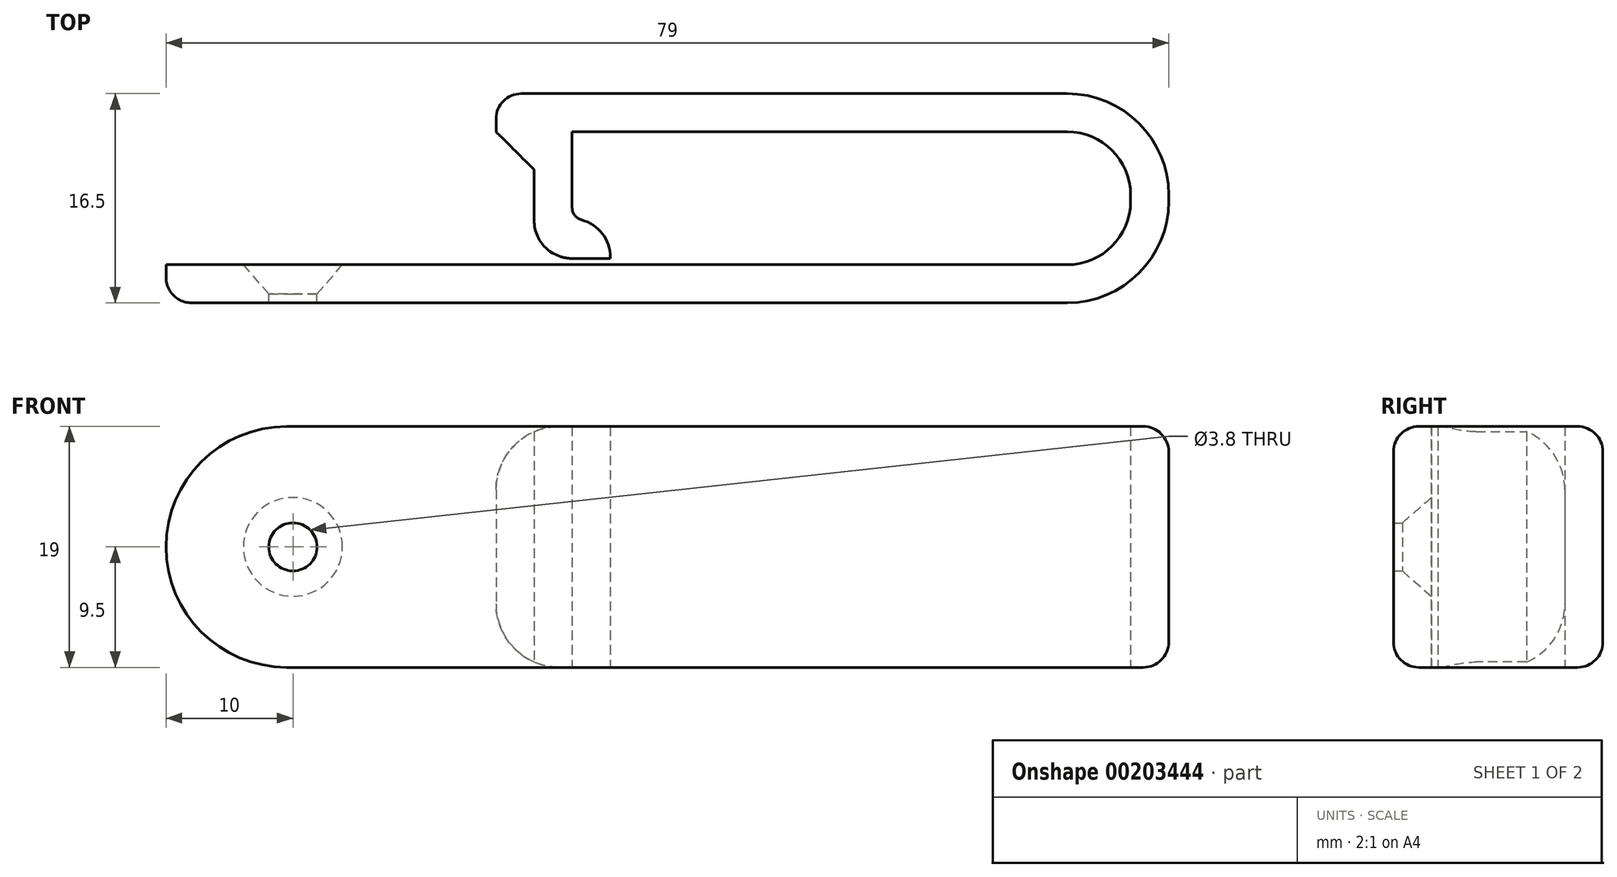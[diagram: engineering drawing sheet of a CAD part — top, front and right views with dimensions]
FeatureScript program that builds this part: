
annotation { "Feature Type Name" : "Feature", "Feature Type Description" : "" }
export const myFeature = defineFeature(function(context is Context, id is Id, definition is map)
    precondition{}
    {
        {
            assignVariable(context, id + "F0", {"name" : "clip_width", "anyValue" : 19});
        }
        {
            assignVariable(context, id + "F1", {"name" : "spur_length", "anyValue" : 3});
        }
        {
            var Q0;
            Q0=qCreatedBy(makeId("Top.planeOp"),FACE);
            var sketch = newSketch(context, id + "F2", { "sketchPlane" : qUnion([Q0])});
            skLineSegment(sketch, "E0", {"start": v(-35.5, -27.86) * mm, "end": v(35.5, -27.86) * mm});
            skLineSegment(sketch, "E1", {"start": v(40.5, -22.86) * mm, "end": v(40.5, -22.36) * mm});
            skLineSegment(sketch, "E2", {"start": v(35.5, -17.36) * mm, "end": v(-3.5, -17.36) * mm});
            skLineSegment(sketch, "E3", {"start": v(-3.5, -17.36) * mm, "end": v(-3.5, -27.36) * mm});
            skLineSegment(sketch, "E4", {"start": v(-3.5, -27.36) * mm, "end": v(-0.5, -27.36) * mm});
            skLineSegment(sketch, "E5", {"start": v(-3.5, -17.36) * mm, "end": v(-6.5, -17.36) * mm});
            skPoint(sketch, "E6.visualSharp", {"position": v(40.5, -27.86) * mm});
            skArc(sketch, "E6.filletArc", {"start": v(35.5, -27.86) * mm, "mid": v(39.04, -26.4) * mm, "end": v(40.5, -22.86) * mm});
            skPoint(sketch, "E7.visualSharp", {"position": v(40.5, -17.36) * mm});
            skArc(sketch, "E7.filletArc", {"start": v(40.5, -22.36) * mm, "mid": v(39.04, -18.82) * mm, "end": v(35.5, -17.36) * mm});
            skLineSegment(sketch, "E8.0", {"start": v(-6.5, -14.36) * mm, "end": v(-9.5, -14.36) * mm});
            skLineSegment(sketch, "E8.1", {"start": v(35.5, -14.36) * mm, "end": v(-6.5, -14.36) * mm});
            skLineSegment(sketch, "E8.2", {"start": v(-35.5, -30.86) * mm, "end": v(35.5, -30.86) * mm});
            skArc(sketch, "E8.3", {"start": v(35.5, -30.86) * mm, "mid": v(41.16, -28.52) * mm, "end": v(43.5, -22.86) * mm});
            skLineSegment(sketch, "E8.4", {"start": v(43.5, -22.86) * mm, "end": v(43.5, -22.36) * mm});
            skArc(sketch, "E8.5", {"start": v(43.5, -22.36) * mm, "mid": v(41.16, -16.7) * mm, "end": v(35.5, -14.36) * mm});
            skLineSegment(sketch, "E9.0", {"start": v(-3.5, -24.36) * mm, "end": v(-0.5, -24.36) * mm});
            skLineSegment(sketch, "E10", {"start": v(-6.5, -17.36) * mm, "end": v(-6.5, -14.36) * mm});
            skLineSegment(sketch, "E11", {"start": v(-0.5, -27.36) * mm, "end": v(-0.5, -24.36) * mm});
            skLineSegment(sketch, "E12", {"start": v(-35.5, -27.86) * mm, "end": v(-35.5, -30.86) * mm});
            skPoint(sketch, "E13", {"position": v(-3.5, -27.36) * mm});
            skLineSegment(sketch, "E14.0", {"start": v(-6.5, -16.36) * mm, "end": v(-6.5, -27.36) * mm});
            skLineSegment(sketch, "E15", {"start": v(-3.5, -27.36) * mm, "end": v(-6.5, -27.36) * mm});
            skLineSegment(sketch, "E16.0", {"start": v(-6.5, -17.36) * mm, "end": v(-9.5, -17.36) * mm});
            skLineSegment(sketch, "E17", {"start": v(-9.5, -17.36) * mm, "end": v(-9.5, -14.36) * mm});
            skPoint(sketch, "E18", {"position": v(-6.5, -21.86) * mm});
            skPoint(sketch, "E19", {"position": v(0, -30.86) * mm});
            skSolve(sketch);
        }
        {
            var Q0;
            Q0=makeQuery(id+"F2.imprint","IMPRINT",FACE,{"disambiguationData":[TD([[makeQuery(id+"F2.imprint","IMPRINT",EDGE,{"derivedFrom":sQuery(id+"F2.wireOp",EDGE,"E0")}),-1.0]])]});
            var Q1;
            {var subQ0=sQuery(id+"F2.wireOp",EDGE,"E4");Q1=makeQuery(id+"F2.imprint","IMPRINT",FACE,{"disambiguationData":[TD([[makeQuery(id+"F2.imprint","IMPRINT",EDGE,{"derivedFrom":subQ0}),1.0]])]});}
            var Q2;
            {var subQ0=sQuery(id+"F2.wireOp",EDGE,"E5");Q2=makeQuery(id+"F2.imprint","IMPRINT",FACE,{"disambiguationData":[TD([[makeQuery(id+"F2.imprint","IMPRINT",EDGE,{"derivedFrom":subQ0}),1.0]])]});}
            var Q3;
            Q3=makeQuery(id+"F2.imprint","IMPRINT",FACE,{"disambiguationData":[TD([[makeQuery(id+"F2.imprint","IMPRINT",EDGE,{"derivedFrom":sQuery(id+"F2.wireOp",EDGE,"E10")}),1.0]])]});
            extrude(context, id + "F3", {"entities" : qUnion([Q0, Q1, Q2, Q3]), "depth" : (getVariable(context, 'clip_width')) * mm});
        }
        {
            var Q0;
            Q0=makeQuery(id+"F3.opExtrude","SWEPT_FACE",FACE,{"disambiguationData":[OSD([sQuery(id+"F2.wireOp",EDGE,"E0")])]});
            var sketch = newSketch(context, id + "F4", { "sketchPlane" : qUnion([Q0])});
            skPoint(sketch, "E20", {"position": v(25.5, 9.5) * mm});
            skPoint(sketch, "E20.positionSnap0", {"position": v(35.5, 9.5) * mm});
            skSolve(sketch);
        }
        {
            var Q0;
            Q0=makeQuery(id+"F3.opExtrude","CAP_EDGE",EDGE,{"disambiguationData":[OSD([sQuery(id+"F2.wireOp",EDGE,"E12")])],"isStart":false});
            var Q1;
            Q1=makeQuery(id+"F3.opExtrude","CAP_EDGE",EDGE,{"disambiguationData":[OSD([sQuery(id+"F2.wireOp",EDGE,"E12")])],"isStart":true});
            fillet(context, id + "F5", {"entities" : qUnion([Q0, Q1]), "radius" : (getVariable(context, 'clip_width') / 2) * mm, "tangentPropagation" : true, "allowEdgeOverflow" : false});
        }
        {
            var Q0;
            Q0=makeQuery(id+"F3.opExtrude","CAP_EDGE",EDGE,{"disambiguationData":[OSD([sQuery(id+"F2.wireOp",EDGE,"E17")])],"isStart":false});
            var Q1;
            Q1=makeQuery(id+"F3.opExtrude","CAP_EDGE",EDGE,{"disambiguationData":[OSD([sQuery(id+"F2.wireOp",EDGE,"E17")])],"isStart":true});
            fillet(context, id + "F6", {"entities" : qUnion([Q0, Q1]), "radius" : 5 * mm, "tangentPropagation" : true, "allowEdgeOverflow" : false});
        }
        {
            var Q0;
            Q0=makeQuery(id+"F3.opExtrude","CAP_EDGE",EDGE,{"disambiguationData":[OSD([sQuery(id+"F2.wireOp",EDGE,"E8.1"),sQuery(id+"F2.wireOp",EDGE,"E8.0")])],"isStart":true});
            fillet(context, id + "F7", {"entities" : qUnion([Q0]), "radius" : 2 * mm, "tangentPropagation" : true, "allowEdgeOverflow" : false});
        }
        {
            var Q0;
            Q0=makeQuery(id+"F3.opExtrude","SWEPT_EDGE",EDGE,{"disambiguationData":[OSD([sQuery(id+"F2.wireOp",EDGE,"E3"),sQuery(id+"F2.wireOp",EDGE,"E9.0")])]});
            fillet(context, id + "F8", {"entities" : qUnion([Q0]), "radius" : 1 * mm, "tangentPropagation" : true, "allowEdgeOverflow" : false});
        }
        {
            var Q0;
            Q0=makeQuery(id+"F3.opExtrude","SWEPT_EDGE",EDGE,{"disambiguationData":[OSD([sQuery(id+"F2.wireOp",EDGE,"E5"),sQuery(id+"F2.wireOp",EDGE,"E10"),sQuery(id+"F2.wireOp",EDGE,"E14.0"),sQuery(id+"F2.wireOp",EDGE,"E16.0")])]});
            chamfer(context, id + "F9", {"entities" : qUnion([Q0]), "width" : (getVariable(context, 'spur_length')) * mm, "tangentPropagation" : true});
        }
        {
            var Q0;
            Q0=sQuery(id+"F4.wireOp",VERTEX,"E20");
            var Q1;
            Q1=makeQuery(id+"F3.opExtrude","SWEPT_BODY",BODY,{"disambiguationData":[OSD([sQuery(id+"F2.wireOp",EDGE,"E0"),sQuery(id+"F2.wireOp",EDGE,"E1"),sQuery(id+"F2.wireOp",EDGE,"E2"),sQuery(id+"F2.wireOp",EDGE,"E3"),sQuery(id+"F2.wireOp",EDGE,"E4"),sQuery(id+"F2.wireOp",EDGE,"E6.filletArc"),sQuery(id+"F2.wireOp",EDGE,"E7.filletArc"),sQuery(id+"F2.wireOp",EDGE,"E8.1"),sQuery(id+"F2.wireOp",EDGE,"E8.2"),sQuery(id+"F2.wireOp",EDGE,"E8.3"),sQuery(id+"F2.wireOp",EDGE,"E8.4"),sQuery(id+"F2.wireOp",EDGE,"E8.5"),sQuery(id+"F2.wireOp",EDGE,"E9.0"),sQuery(id+"F2.wireOp",EDGE,"E11"),sQuery(id+"F2.wireOp",EDGE,"E12"),sQuery(id+"F2.wireOp",EDGE,"E14.0"),sQuery(id+"F2.wireOp",EDGE,"E15"),sQuery(id+"F2.wireOp",EDGE,"E8.0"),sQuery(id+"F2.wireOp",EDGE,"E16.0"),sQuery(id+"F2.wireOp",EDGE,"E17")])]});
            hole(context, id + "F10", {"style" : HoleStyle.C_SINK, "endStyle" : HoleEndStyle.THROUGH, "standardTappedOrClearance" : lookupTablePath({ "standard" : "ANSI", "fit" : "Normal (ASME)", "size" : "#6", "type" : "Clearance" }), "standardBlindInLast" : lookupTablePath({ "fit" : "Free", "standard" : "ANSI", "size" : "#6", "type" : "Clearance" }), "holeDiameter" : 3.8 * mm, "cSinkDiameter" : 7.8 * mm, "cSinkAngle" : 82 * degree, "tappedDepth" : 12 * mm, "tapClearance" : 3, "locations" : qUnion([Q0]), "scope" : qUnion([Q1])});
        }
        {
            var Q0;
            Q0=makeQuery(id+"F3.opExtrude","SWEPT_EDGE",EDGE,{"disambiguationData":[OSD([sQuery(id+"F2.wireOp",EDGE,"E9.0"),sQuery(id+"F2.wireOp",EDGE,"E11")])]});
            var Q1;
            Q1=makeQuery(id+"F3.opExtrude","SWEPT_EDGE",EDGE,{"disambiguationData":[OSD([sQuery(id+"F2.wireOp",EDGE,"E14.0"),sQuery(id+"F2.wireOp",EDGE,"E15")])]});
            fillet(context, id + "F11", {"entities" : qUnion([Q0, Q1]), "radius" : (getVariable(context, 'spur_length')) * mm, "tangentPropagation" : true, "allowEdgeOverflow" : false});
        }
    });
